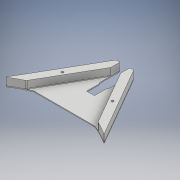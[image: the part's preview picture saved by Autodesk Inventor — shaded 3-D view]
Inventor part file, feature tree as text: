
AUTODESK INVENTOR PART (.ipt)
format: ipt  version: 2018 (Build 220112000, 112)  size: 228,352 bytes
history: native  units: mm
features: fillet x12, sketch x3, extrude x2, hole x1
ambient origin geometry x8: Origin, YZ Plane, XZ Plane, XY Plane, X Axis, Y Axis, Z Axis, Center Point
bodies: Solid1 (feature_tree)
feature tree (18):
  extrude  "Extrusion1"  Depth=175.866199mm
  extrude  "Extrusion2"  Depth=175.886mm
  hole  "Hole1"  [1 undecoded]
  fillet  "Fillet1"  Radius=8.254mm
  fillet  "Fillet2"  Radius=19.704mm
  fillet  "Fillet3"  [1 undecoded]
  fillet  "Fillet4"  Radius=16.0mm
  fillet  "Fillet5"  Radius=376.0mm
  fillet  "Fillet6"  Radius=21.750293mm
  fillet  "Fillet7"  Radius=175.886mm
  fillet  "Fillet8"  [1 undecoded]
  fillet  "Fillet9"  Radius=10.0mm
  fillet  "Fillet10"  Radius=87.943mm
  fillet  "Fillet11"  [1 undecoded]
  fillet  "Fillet12"  Radius=5.0mm
  sketch  "Sketch1"  dims[d40=2.0mm d41=0.0mm d48=175.866199mm]
  sketch  "Sketch2"  dims[d49=8.253944mm d50=175.886mm]
  sketch  "Sketch3"  dims[d52=8.254mm d56=19.703653mm d58=8.254mm d59=19.704mm d60=150.0deg d61=16.0mm d62=0.0mm d63=376.0mm d64=21.750293mm d65=175.886mm d66=60.0deg d67=10.0mm d68=87.943mm d69=120.0deg d70=5.0mm d71=6.0mm d72=10.0mm d73=13.0mm d74=90.0deg d75=18.0mm d76=20.594885mm d77=5.0mm d78=5.0mm d79=2.0mm d80=5.0mm d81=2.0mm d82=5.0mm d83=5.0mm d84=0.5mm d85=0.5mm d86=0.5mm d87=1.0mm d88=1.0mm]
note: 4 required parameter values undecoded (feature->parameter linkage not recoverable at this tier; creation-order binding heuristic only, values carry confidence <= 0.55)
